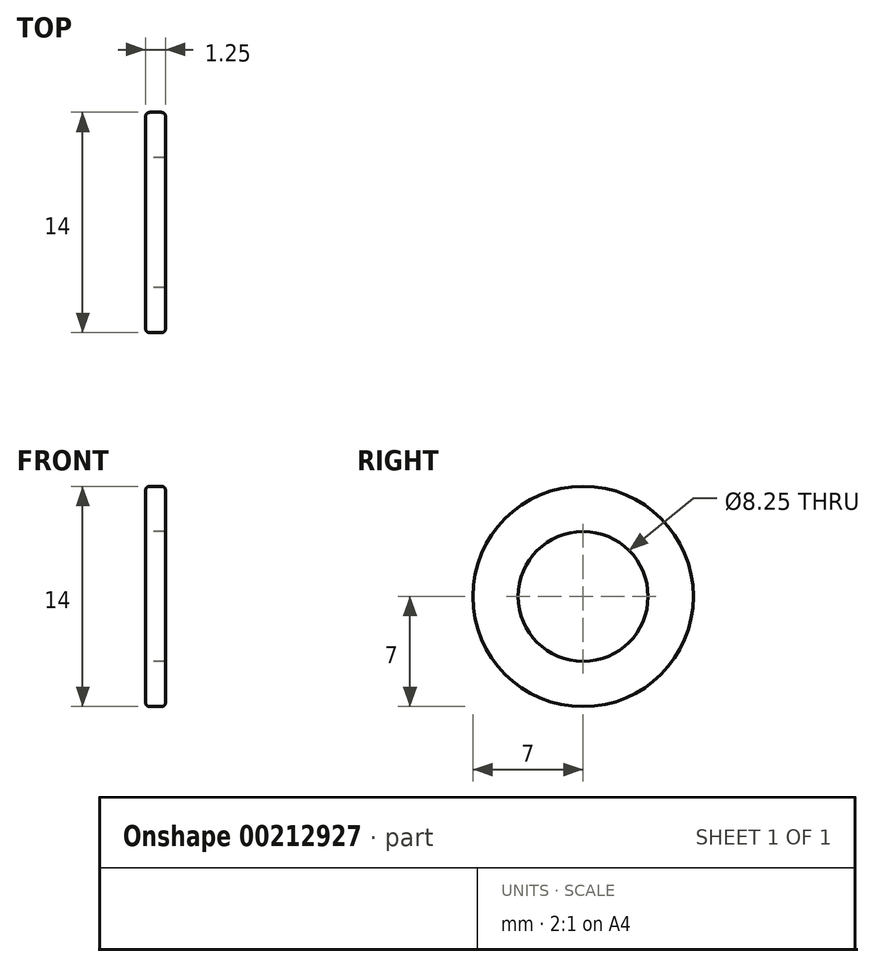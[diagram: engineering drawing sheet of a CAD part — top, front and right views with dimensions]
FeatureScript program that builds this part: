
annotation { "Feature Type Name" : "Feature", "Feature Type Description" : "" }
export const myFeature = defineFeature(function(context is Context, id is Id, definition is map)
    precondition{}
    {
        {
            var Q0;
            Q0=qCreatedBy(makeId("Right.planeOp"),FACE);
            var sketch = newSketch(context, id + "F0", { "sketchPlane" : qUnion([Q0])});
            skCircle(sketch, "E0", {"center": v(0, 0) * mm, "radius": 7 * mm});
            skCircle(sketch, "E1", {"center": v(0, 0) * mm, "radius": 4 * mm});
            skCircle(sketch, "E2", {"center": v(0, 0) * mm, "radius": 4.12 * mm});
            skSolve(sketch);
        }
        {
            var Q0;
            Q0=makeQuery(id+"F0.imprint","IMPRINT",FACE,{"disambiguationData":[TD([[makeQuery(id+"F0.imprint","IMPRINT",EDGE,{"derivedFrom":sQuery(id+"F0.wireOp",EDGE,"E0")}),1.0]])]});
            extrude(context, id + "F1", {"entities" : qUnion([Q0]), "depth" : 1.25 * mm});
        }
        {
            var Q0;
            Q0=sQuery(id+"F0.wireOp",EDGE,"E2");
            var Q1;
            Q1=sQuery(id+"F0.wireOp",EDGE,"E1");
            extrude(context, id + "F2", {"bodyType" : ToolBodyType.SURFACE, "surfaceEntities" : qUnion([Q0, Q1]), "oppositeDirection" : true, "depth" : 1 * mm});
        }
        {
            var Q0;
            Q0=makeQuery(id+"F1.opExtrude","CAP_EDGE",EDGE,{"disambiguationData":[OSD([sQuery(id+"F0.wireOp",EDGE,"E0")])],"isStart":false});
            var Q1;
            Q1=makeQuery(id+"F1.opExtrude","CAP_EDGE",EDGE,{"disambiguationData":[OSD([sQuery(id+"F0.wireOp",EDGE,"E0")])],"isStart":true});
            fillet(context, id + "F3", {"entities" : qUnion([Q0, Q1]), "radius" : .25 * mm, "tangentPropagation" : true, "allowEdgeOverflow" : false});
        }
    });
